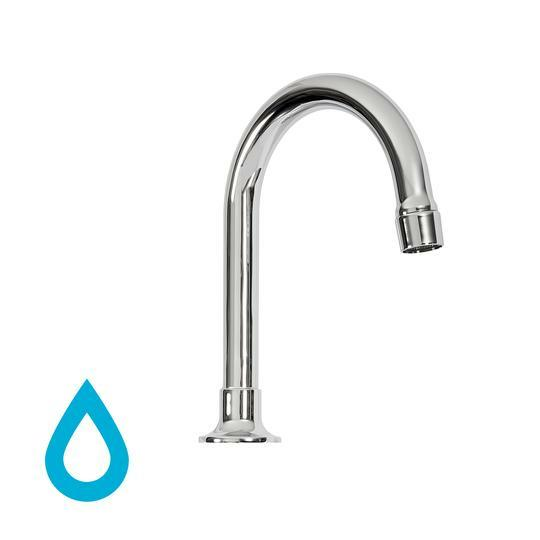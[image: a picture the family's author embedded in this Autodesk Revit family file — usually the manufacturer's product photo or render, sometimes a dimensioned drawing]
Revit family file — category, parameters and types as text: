
# Revit family: II-BR04-11-BRAZO FIJO LAVAMANOS
name_source: partatom
category: Plumbing Fixtures
revit_build: Autodesk Revit 2018 (Build: 20170223_1515(x64)
units: mm (PartAtom-declared; Revit-internal decimal feet)

## family parameters
Cut with Voids When Loaded = No
Host = Face
OmniClass Number = 23.31.11.00
Part Type = Normal
Room Calculation Point = No
Round Connector Dimension = Use Diameter
Shared = No

## types (1)
- II-BR04-11
    Alto = 235 mm  [stored 0.770997 ft]
    Ancho = 54 mm  [stored 0.177165 ft]
    CW Connection = Yes
    Default Elevation = 0 mm  [stored 0 ft]
    Description = Brazo Griferia Lavamanos
    HW Connection = Yes
    Link Ficha Tecnica = https://infotecnica.gricol.com
    Manufacturer = Gricol
    Model = II-BR04-11
    Plastico ABS Cromado = Metal Laton Cromado
    Product Name = BRAZO FIJO LAVAMANOS
    Profundidad = 125 mm
    Type Image = FOTO BRAZO FIJO LAVAMANOS.jpg
    URL = https://www.gricol.com
    Vent Connection = No
    Waste Connection = No

note: [stored X ft] marks values corroborated as IEEE doubles in the binary element streams (Revit-internal decimal feet)

## geometry (parser evidence)
native form markers: Blend x2, Sweep x3
no freeform markers — native parametric forms only
